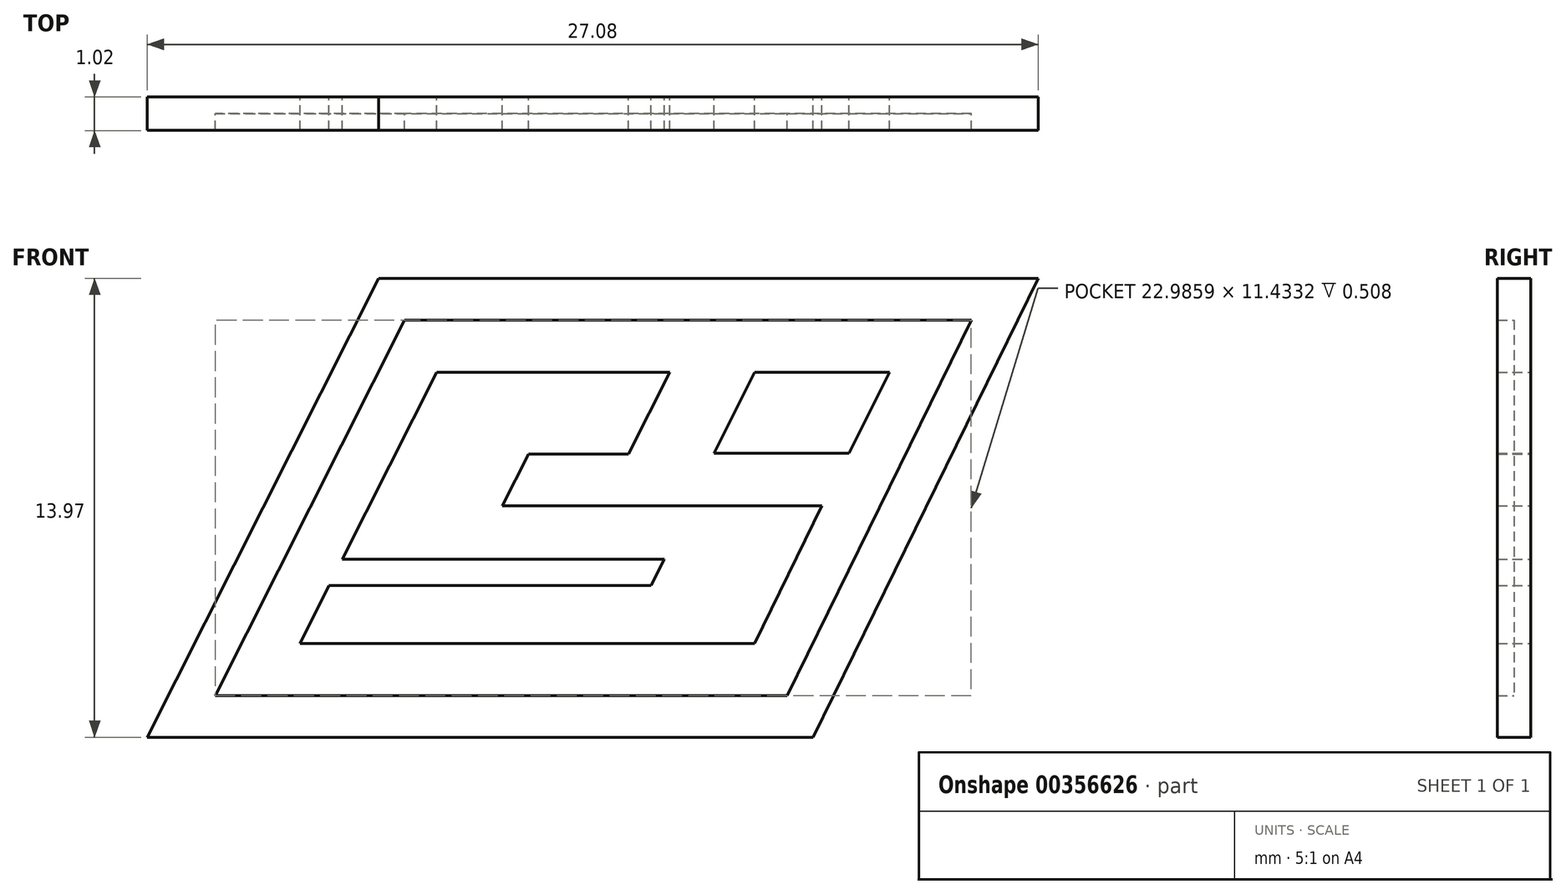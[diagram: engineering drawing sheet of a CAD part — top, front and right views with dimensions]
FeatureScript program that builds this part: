
annotation { "Feature Type Name" : "Feature", "Feature Type Description" : "" }
export const myFeature = defineFeature(function(context is Context, id is Id, definition is map)
    precondition{}
    {
        {
            var Q0;
            Q0=qCreatedBy(makeId("Front.planeOp"),FACE);
            var sketch = newSketch(context, id + "F0", { "sketchPlane" : qUnion([Q0])});
            skLineSegment(sketch, "E0", {"start": v(-12.43, 33) * mm, "end": v(15.1, 33) * mm, "construction": true});
            skLineSegment(sketch, "E1", {"start": v(15.1, 33) * mm, "end": v(6.9, 16.48) * mm, "construction": true});
            skLineSegment(sketch, "E2", {"start": v(6.9, 16.48) * mm, "end": v(-20.75, 16.48) * mm, "construction": true});
            skLineSegment(sketch, "E3", {"start": v(-20.75, 16.48) * mm, "end": v(-12.43, 33) * mm, "construction": true});
            skLineSegment(sketch, "E4", {"start": v(-12.43, 33) * mm, "end": v(1.74, 33) * mm});
            skLineSegment(sketch, "E5", {"start": v(1.74, 33) * mm, "end": v(-0.77, 28.01) * mm});
            skLineSegment(sketch, "E6", {"start": v(-0.77, 28.01) * mm, "end": v(-6.84, 28.01) * mm});
            skLineSegment(sketch, "E7", {"start": v(-6.84, 28.01) * mm, "end": v(-8.43, 24.86) * mm});
            skLineSegment(sketch, "E8", {"start": v(-8.43, 24.86) * mm, "end": v(11, 24.86) * mm});
            skPoint(sketch, "E8.endSnap0", {"position": v(11, 24.74) * mm});
            skLineSegment(sketch, "E9", {"start": v(11, 24.86) * mm, "end": v(6.9, 16.48) * mm});
            skLineSegment(sketch, "E10", {"start": v(-20.75, 16.48) * mm, "end": v(-18.97, 20) * mm});
            skLineSegment(sketch, "E11", {"start": v(-18.97, 20) * mm, "end": v(0.6, 20) * mm});
            skLineSegment(sketch, "E12", {"start": v(0.6, 20) * mm, "end": v(1.4, 21.6) * mm});
            skLineSegment(sketch, "E13", {"start": v(1.4, 21.6) * mm, "end": v(-18.16, 21.6) * mm});
            skLineSegment(sketch, "E14", {"start": v(-18.16, 21.6) * mm, "end": v(-12.43, 33) * mm});
            skLineSegment(sketch, "E15", {"start": v(6.9, 33) * mm, "end": v(4.45, 28.06) * mm});
            skLineSegment(sketch, "E16", {"start": v(4.45, 28.06) * mm, "end": v(12.65, 28.06) * mm});
            skLineSegment(sketch, "E17", {"start": v(12.65, 28.06) * mm, "end": v(15.1, 33) * mm});
            skLineSegment(sketch, "E18", {"start": v(-20.75, 16.48) * mm, "end": v(6.9, 16.48) * mm});
            skLineSegment(sketch, "E19", {"start": v(6.9, 33) * mm, "end": v(15.1, 33) * mm});
            skSolve(sketch);
        }
        {
            var Q0;
            Q0=qCreatedBy(makeId("Front.planeOp"),FACE);
            var sketch = newSketch(context, id + "F1", { "sketchPlane" : qUnion([Q0])});
            skLineSegment(sketch, "E20", {"start": v(-25.9, 13.3) * mm, "end": v(8.88, 13.3) * mm});
            skLineSegment(sketch, "E21", {"start": v(8.88, 13.3) * mm, "end": v(20.07, 36.17) * mm});
            skLineSegment(sketch, "E22", {"start": v(20.07, 36.17) * mm, "end": v(-14.38, 36.17) * mm});
            skLineSegment(sketch, "E23", {"start": v(-14.38, 36.17) * mm, "end": v(-25.9, 13.3) * mm});
            skSolve(sketch);
        }
        {
            var Q0;
            Q0=qCreatedBy(makeId("Front.planeOp"),FACE);
            var sketch = newSketch(context, id + "F2", { "sketchPlane" : qUnion([Q0])});
            skLineSegment(sketch, "E24", {"start": v(-30.02, 10.77) * mm, "end": v(-15.95, 38.71) * mm});
            skLineSegment(sketch, "E25", {"start": v(-15.95, 38.71) * mm, "end": v(24.14, 38.71) * mm});
            skLineSegment(sketch, "E26", {"start": v(24.14, 38.71) * mm, "end": v(10.47, 10.77) * mm});
            skLineSegment(sketch, "E27", {"start": v(10.47, 10.77) * mm, "end": v(-30.02, 10.77) * mm});
            skLineSegment(sketch, "E28.0", {"start": v(8.88, 13.3) * mm, "end": v(20.07, 36.17) * mm});
            skLineSegment(sketch, "E29.0", {"start": v(20.07, 36.17) * mm, "end": v(-14.38, 36.17) * mm});
            skLineSegment(sketch, "E30.0", {"start": v(-14.38, 36.17) * mm, "end": v(-25.9, 13.3) * mm});
            skLineSegment(sketch, "E31.0", {"start": v(-25.9, 13.3) * mm, "end": v(8.88, 13.3) * mm});
            skSolve(sketch);
        }
        {
            var Q0;
            Q0=makeQuery(id+"F0.imprint","IMPRINT",FACE,{"disambiguationData":[TD([[makeQuery(id+"F0.imprint","IMPRINT",EDGE,{"derivedFrom":sQuery(id+"F0.wireOp",EDGE,"E4")}),-1.0]])]});
            var Q1;
            Q1=makeQuery(id+"F0.imprint","IMPRINT",FACE,{"disambiguationData":[TD([[makeQuery(id+"F0.imprint","IMPRINT",EDGE,{"derivedFrom":sQuery(id+"F0.wireOp",EDGE,"E15")}),1.0]])]});
            extrude(context, id + "F3", {"entities" : qUnion([Q0, Q1]), "offsetDistance" : 25.4 * mm, "depth" : 2.03 * mm});
        }
        {
            var Q0;
            Q0=makeQuery(id+"F1.imprint","IMPRINT",FACE,{"disambiguationData":[TD([[makeQuery(id+"F1.imprint","IMPRINT",EDGE,{"derivedFrom":sQuery(id+"F1.wireOp",EDGE,"E20")}),1.0]])]});
            extrude(context, id + "F4", {"entities" : qUnion([Q0]), "offsetDistance" : 25.4 * mm, "depth" : 1.02 * mm});
        }
        {
            var Q0;
            Q0=makeQuery(id+"F2.imprint","IMPRINT",FACE,{"disambiguationData":[TD([[makeQuery(id+"F2.imprint","IMPRINT",EDGE,{"derivedFrom":sQuery(id+"F2.wireOp",EDGE,"E24")}),-1.0]])]});
            extrude(context, id + "F5", {"entities" : qUnion([Q0]), "operationType" : NewBodyOperationType.ADD, "offsetDistance" : 25.4 * mm, "depth" : 2.03 * mm});
        }
        {
            var Q0;
            Q0=makeQuery(id+"F4.opExtrude","SWEPT_BODY",BODY,{"disambiguationData":[OSD([sQuery(id+"F1.wireOp",EDGE,"E20"),sQuery(id+"F1.wireOp",EDGE,"E21"),sQuery(id+"F1.wireOp",EDGE,"E22"),sQuery(id+"F1.wireOp",EDGE,"E23")])]});
            var Q1;
            Q1=makeQuery(id+"F3.opExtrude","SWEPT_BODY",BODY,{"disambiguationData":[OSD([sQuery(id+"F0.wireOp",EDGE,"E4"),sQuery(id+"F0.wireOp",EDGE,"E5"),sQuery(id+"F0.wireOp",EDGE,"E6"),sQuery(id+"F0.wireOp",EDGE,"E7"),sQuery(id+"F0.wireOp",EDGE,"E8"),sQuery(id+"F0.wireOp",EDGE,"E9"),sQuery(id+"F0.wireOp",EDGE,"E10"),sQuery(id+"F0.wireOp",EDGE,"E11"),sQuery(id+"F0.wireOp",EDGE,"E12"),sQuery(id+"F0.wireOp",EDGE,"E13"),sQuery(id+"F0.wireOp",EDGE,"E14"),sQuery(id+"F0.wireOp",EDGE,"E18")])]});
            var Q2;
            Q2=makeQuery(id+"F3.opExtrude","SWEPT_BODY",BODY,{"disambiguationData":[OSD([sQuery(id+"F0.wireOp",EDGE,"E15"),sQuery(id+"F0.wireOp",EDGE,"E16"),sQuery(id+"F0.wireOp",EDGE,"E17"),sQuery(id+"F0.wireOp",EDGE,"E19")])]});
            var Q3;
            Q3=sQuery(id+"F0.wireOp",VERTEX,"E7.start");
            transform(context, id + "F6", {"entities" : qUnion([Q0, Q1, Q2]), "transformType" : TransformType.SCALE_UNIFORMLY, "scale" : .5, "scalePoint" : qUnion([Q3]), "makeCopy" : false});
        }
    });
